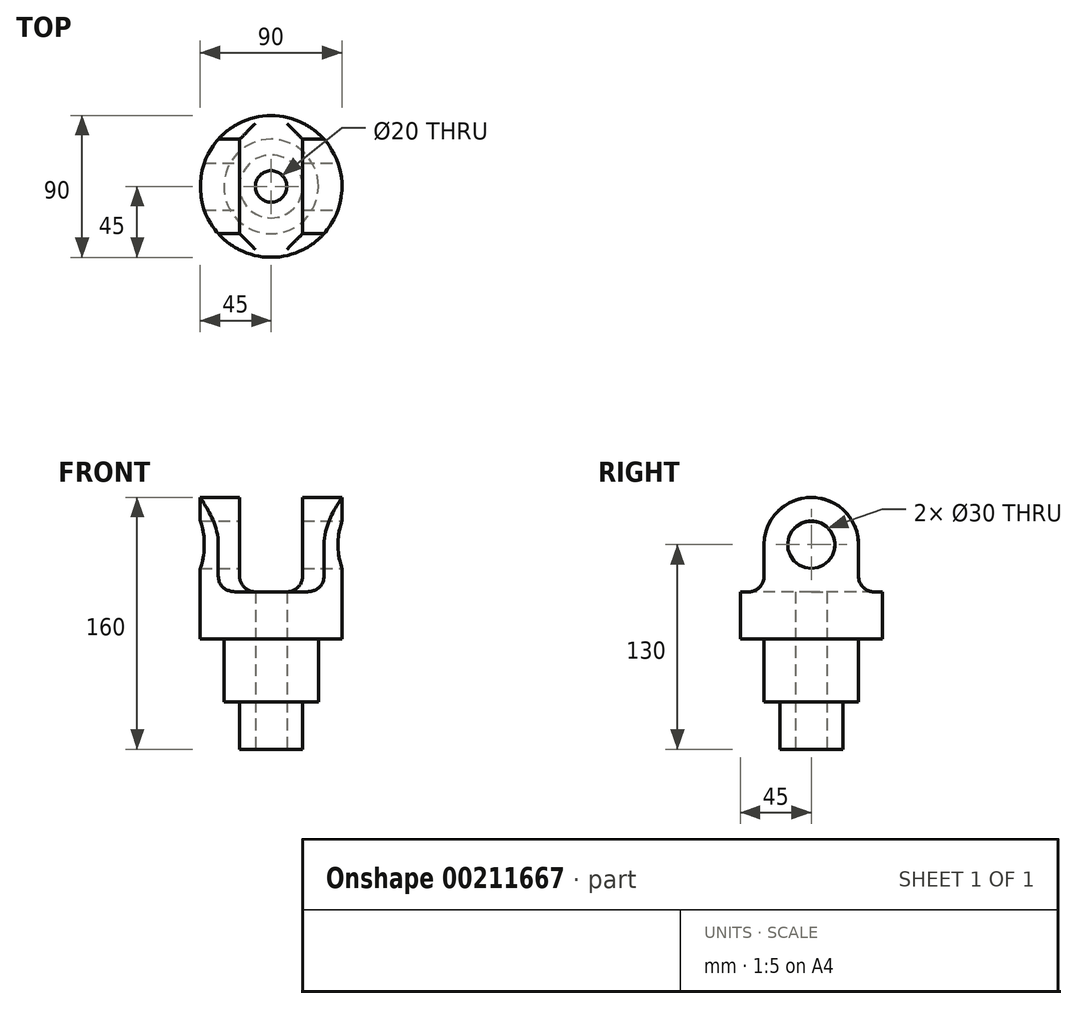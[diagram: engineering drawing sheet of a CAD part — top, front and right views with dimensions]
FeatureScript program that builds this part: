
annotation { "Feature Type Name" : "Feature", "Feature Type Description" : "" }
export const myFeature = defineFeature(function(context is Context, id is Id, definition is map)
    precondition{}
    {
        {
            var Q0;
            Q0=qCreatedBy(makeId("Top.planeOp"),FACE);
            var sketch = newSketch(context, id + "F0", { "sketchPlane" : qUnion([Q0])});
            skCircle(sketch, "E0", {"center": v(0, 0) * mm, "radius": 45 * mm});
            skCircle(sketch, "E1", {"center": v(0, 0) * mm, "radius": 30 * mm});
            skCircle(sketch, "E2", {"center": v(0, 0) * mm, "radius": 20 * mm});
            skSolve(sketch);
        }
        {
            var Q0;
            Q0=makeQuery(id+"F0.imprint","IMPRINT",FACE,{"disambiguationData":[TD([[makeQuery(id+"F0.imprint","IMPRINT",EDGE,{"derivedFrom":sQuery(id+"F0.wireOp",EDGE,"E2")}),1.0]])]});
            var Q1;
            Q1=makeQuery(id+"F0.imprint","IMPRINT",FACE,{"disambiguationData":[TD([[makeQuery(id+"F0.imprint","IMPRINT",EDGE,{"derivedFrom":sQuery(id+"F0.wireOp",EDGE,"E1")}),1.0]])]});
            var Q2;
            Q2=makeQuery(id+"F0.imprint","IMPRINT",FACE,{"disambiguationData":[TD([[makeQuery(id+"F0.imprint","IMPRINT",EDGE,{"derivedFrom":sQuery(id+"F0.wireOp",EDGE,"E0")}),1.0]])]});
            extrude(context, id + "F1", {"entities" : qUnion([Q0, Q1, Q2]), "depth" : 90 * mm});
        }
        {
            var Q0;
            Q0=makeQuery(id+"F0.imprint","IMPRINT",FACE,{"disambiguationData":[TD([[makeQuery(id+"F0.imprint","IMPRINT",EDGE,{"derivedFrom":sQuery(id+"F0.wireOp",EDGE,"E2")}),1.0]])]});
            extrude(context, id + "F2", {"entities" : qUnion([Q0]), "operationType" : NewBodyOperationType.ADD, "oppositeDirection" : true, "depth" : 70 * mm});
        }
        {
            var Q0;
            Q0=makeQuery(id+"F0.imprint","IMPRINT",FACE,{"disambiguationData":[TD([[makeQuery(id+"F0.imprint","IMPRINT",EDGE,{"derivedFrom":sQuery(id+"F0.wireOp",EDGE,"E1")}),1.0]])]});
            extrude(context, id + "F3", {"entities" : qUnion([Q0]), "operationType" : NewBodyOperationType.ADD, "oppositeDirection" : true, "depth" : 40 * mm});
        }
        {
            var Q0;
            Q0=qCreatedBy(makeId("Right.planeOp"),FACE);
            var sketch = newSketch(context, id + "F4", { "sketchPlane" : qUnion([Q0])});
            skLineSegment(sketch, "E3", {"start": v(-82.79, 30) * mm, "end": v(-40, 30) * mm});
            skLineSegment(sketch, "E4", {"start": v(-30, 40) * mm, "end": v(-30, 60) * mm});
            skArc(sketch, "E5", {"start": v(30, 60) * mm, "mid": v(0, 90) * mm, "end": v(-30, 60) * mm});
            skPoint(sketch, "E6.visualSharp", {"position": v(-30, 30) * mm});
            skArc(sketch, "E6.filletArc", {"start": v(-40, 30) * mm, "mid": v(-32.93, 32.93) * mm, "end": v(-30, 40) * mm});
            skLineSegment(sketch, "E7.MirrorCS", {"start": v(30, 40) * mm, "end": v(30, 60) * mm});
            skLineSegment(sketch, "E8.MirrorCS", {"start": v(82.79, 30) * mm, "end": v(40, 30) * mm});
            skArc(sketch, "E9.MirrorCS", {"start": v(40, 30) * mm, "mid": v(32.93, 32.93) * mm, "end": v(30, 40) * mm});
            skLineSegment(sketch, "E10", {"start": v(-82.79, 30) * mm, "end": v(-82.79, 115.94) * mm});
            skLineSegment(sketch, "E11", {"start": v(-82.79, 115.94) * mm, "end": v(82.79, 115.94) * mm});
            skLineSegment(sketch, "E12", {"start": v(82.79, 115.94) * mm, "end": v(82.79, 30) * mm});
            skCircle(sketch, "E13", {"center": v(0, 60) * mm, "radius": 15 * mm});
            skSolve(sketch);
        }
        {
            var Q0;
            Q0=makeQuery(id+"F4.imprint","IMPRINT",FACE,{"disambiguationData":[TD([[makeQuery(id+"F4.imprint","IMPRINT",EDGE,{"derivedFrom":sQuery(id+"F4.wireOp",EDGE,"E3")}),1.0]])]});
            extrude(context, id + "F5", {"entities" : qUnion([Q0]), "operationType" : NewBodyOperationType.REMOVE, "endBound" : BoundingType.SYMMETRIC, "oppositeDirection" : true, "depth" : 100 * mm});
        }
        {
            var Q0;
            Q0=makeQuery(id+"F4.imprint","IMPRINT",FACE,{"disambiguationData":[TD([[makeQuery(id+"F4.imprint","IMPRINT",EDGE,{"derivedFrom":sQuery(id+"F4.wireOp",EDGE,"E13")}),1.0]])]});
            extrude(context, id + "F6", {"entities" : qUnion([Q0]), "operationType" : NewBodyOperationType.REMOVE, "endBound" : BoundingType.SYMMETRIC, "oppositeDirection" : true, "depth" : 100 * mm});
        }
        {
            var Q0;
            Q0=qCreatedBy(makeId("Front.planeOp"),FACE);
            var sketch = newSketch(context, id + "F7", { "sketchPlane" : qUnion([Q0])});
            skLineSegment(sketch, "E14.bottom", {"start": v(-20, 128.13) * mm, "end": v(20, 128.13) * mm});
            skLineSegment(sketch, "E14.top", {"start": v(-10, 30) * mm, "end": v(10, 30) * mm});
            skLineSegment(sketch, "E14.left", {"start": v(-20, 128.13) * mm, "end": v(-20, 40) * mm});
            skLineSegment(sketch, "E14.right", {"start": v(20, 128.13) * mm, "end": v(20, 40) * mm});
            skPoint(sketch, "E15.visualSharp", {"position": v(-20, 30) * mm});
            skArc(sketch, "E15.filletArc", {"start": v(-20, 40) * mm, "mid": v(-17.07, 32.93) * mm, "end": v(-10, 30) * mm});
            skPoint(sketch, "E16.visualSharp", {"position": v(20, 30) * mm});
            skArc(sketch, "E16.filletArc", {"start": v(10, 30) * mm, "mid": v(17.07, 32.93) * mm, "end": v(20, 40) * mm});
            skSolve(sketch);
        }
        {
            var Q0;
            Q0=makeQuery(id+"F7.imprint","IMPRINT",FACE,{"disambiguationData":[TD([[makeQuery(id+"F7.imprint","IMPRINT",EDGE,{"derivedFrom":sQuery(id+"F7.wireOp",EDGE,"E14.bottom")}),-1.0]])]});
            extrude(context, id + "F8", {"entities" : qUnion([Q0]), "operationType" : NewBodyOperationType.REMOVE, "endBound" : BoundingType.SYMMETRIC, "oppositeDirection" : true, "depth" : 100 * mm});
        }
        {
            var Q0;
            Q0=makeQuery(id+"F2.opExtrude","CAP_FACE",FACE,{"disambiguationData":[OSD([sQuery(id+"F0.wireOp",EDGE,"E2")])],"isStart":false});
            var sketch = newSketch(context, id + "F9", { "sketchPlane" : qUnion([Q0])});
            skPoint(sketch, "E17", {"position": v(0, 0) * mm});
            skSolve(sketch);
        }
        {
            var Q0;
            Q0=sQuery(id+"F9.wireOp",VERTEX,"E17");
            var Q1;
            Q1=makeQuery(id+"F1.opExtrude","SWEPT_BODY",BODY,{"disambiguationData":[OSD([sQuery(id+"F0.wireOp",EDGE,"E0")])]});
            hole(context, id + "F10", {"style" : HoleStyle.SIMPLE, "endStyle" : HoleEndStyle.THROUGH, "holeDiameter" : 20 * mm, "locations" : qUnion([Q0]), "scope" : qUnion([Q1]), "isTappedThrough" : true});
        }
    });
